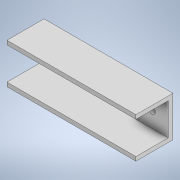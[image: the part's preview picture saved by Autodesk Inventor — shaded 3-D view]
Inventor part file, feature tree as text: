
AUTODESK INVENTOR PART (.ipt)
format: ipt  version: 2021 (Build 250183000, 183)  size: 120,320 bytes
history: native  units: mm
features: extrude x2, sketch x2, projected_geometry x1
ambient origin geometry x8: Origin, YZ Plane, XZ Plane, XY Plane, X Axis, Y Axis, Z Axis, Center Point
bodies: Solid1 (feature_tree)
feature tree (5):
  extrude  "Extrusion1"  Depth=80.0mm
  extrude  "Extrusion2"  Depth=2.5mm
  sketch  "Sketch1"  dims[d0=25.0mm d1=80.0mm]
  sketch  "Sketch2"  dims[d2=3.0mm d3=0.0mm d4=2.5mm d5=2.5mm d6=20.0mm d7=20.0mm d8=0.0mm d9=4.3mm d10=5.0mm d11=5.0mm d12=10.0mm d13=10.0mm]
  projected_geometry  "Projected Loop1"
